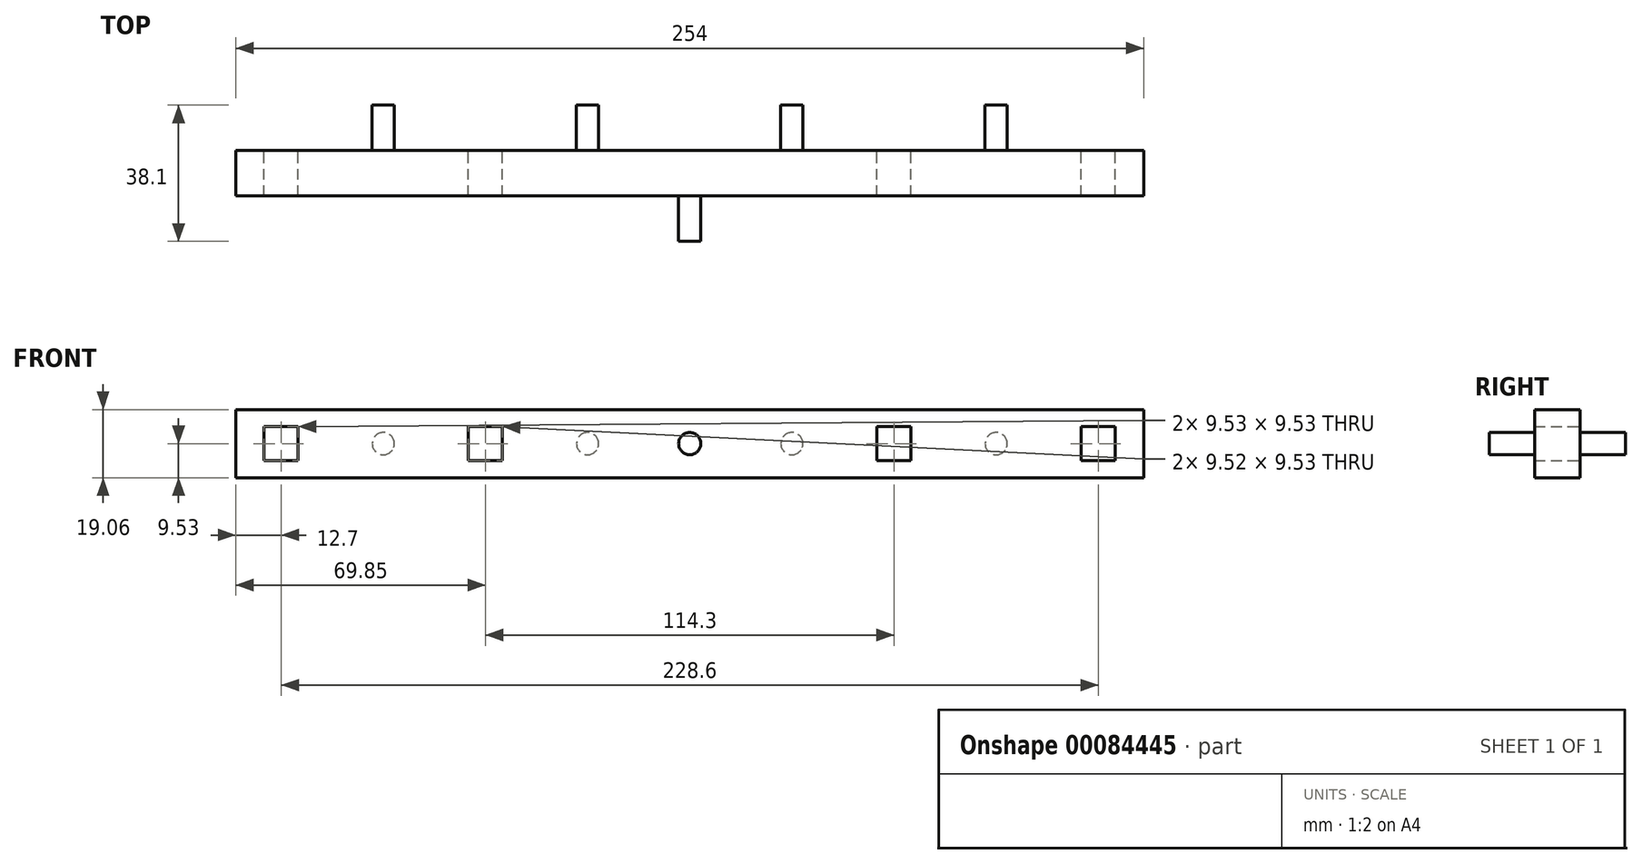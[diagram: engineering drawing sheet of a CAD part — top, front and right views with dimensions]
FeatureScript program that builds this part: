
annotation { "Feature Type Name" : "Feature", "Feature Type Description" : "" }
export const myFeature = defineFeature(function(context is Context, id is Id, definition is map)
    precondition{}
    {
        {
            var Q0;
            Q0=qCreatedBy(makeId("Front.planeOp"),FACE);
            var sketch = newSketch(context, id + "F0", { "sketchPlane" : qUnion([Q0])});
            skLineSegment(sketch, "E0.bottom", {"start": v(127, 9.53) * mm, "end": v(-127, 9.53) * mm});
            skLineSegment(sketch, "E0.top", {"start": v(127, -9.53) * mm, "end": v(-127, -9.53) * mm});
            skLineSegment(sketch, "E0.left", {"start": v(127, 9.53) * mm, "end": v(127, -9.53) * mm});
            skLineSegment(sketch, "E0.right", {"start": v(-127, 9.53) * mm, "end": v(-127, -9.53) * mm});
            skPoint(sketch, "E0.middle", {"position": v(0, 0) * mm});
            skSolve(sketch);
        }
        {
            var Q0;
            Q0 = qSketchRegion(id + "F0", true);
            extrude(context, id + "F1", {"entities" : qUnion([Q0]), "depth" : 12.7 * mm});
        }
        {
            var Q0;
            Q0=makeQuery(id+"F1.opExtrude","CAP_FACE",FACE,{"disambiguationData":[OSD([sQuery(id+"F0.wireOp",EDGE,"E0.bottom"),sQuery(id+"F0.wireOp",EDGE,"E0.top"),sQuery(id+"F0.wireOp",EDGE,"E0.left"),sQuery(id+"F0.wireOp",EDGE,"E0.right")])],"isStart":false});
            var sketch = newSketch(context, id + "F2", { "sketchPlane" : qUnion([Q0])});
            skCircle(sketch, "E1", {"center": v(0, 0) * mm, "radius": 3.11 * mm});
            skSolve(sketch);
        }
        {
            var Q0;
            Q0=makeQuery(id+"F2.imprint","IMPRINT",FACE,{"disambiguationData":[TD([[makeQuery(id+"F2.imprint","IMPRINT",EDGE,{"derivedFrom":sQuery(id+"F2.wireOp",EDGE,"E1")}),1.0]])]});
            extrude(context, id + "F3", {"entities" : qUnion([Q0]), "operationType" : NewBodyOperationType.ADD, "depth" : 12.7 * mm});
        }
        {
            var Q0;
            Q0=makeQuery(id+"F1.opExtrude","CAP_FACE",FACE,{"disambiguationData":[OSD([sQuery(id+"F0.wireOp",EDGE,"E0.bottom"),sQuery(id+"F0.wireOp",EDGE,"E0.top"),sQuery(id+"F0.wireOp",EDGE,"E0.left"),sQuery(id+"F0.wireOp",EDGE,"E0.right")])],"isStart":true});
            var sketch = newSketch(context, id + "F4", { "sketchPlane" : qUnion([Q0])});
            skPoint(sketch, "E2.middle", {"position": v(0, 0) * mm});
            skLineSegment(sketch, "E3.bottom", {"start": v(61.91, -4.76) * mm, "end": v(52.39, -4.76) * mm});
            skLineSegment(sketch, "E3.top", {"start": v(61.91, 4.76) * mm, "end": v(52.39, 4.76) * mm});
            skLineSegment(sketch, "E3.left", {"start": v(61.91, -4.76) * mm, "end": v(61.91, 4.76) * mm});
            skLineSegment(sketch, "E3.right", {"start": v(52.39, -4.76) * mm, "end": v(52.39, 4.76) * mm});
            skPoint(sketch, "E3.middle", {"position": v(57.15, 0) * mm});
            skLineSegment(sketch, "E4.bottom", {"start": v(-52.39, -4.76) * mm, "end": v(-61.91, -4.76) * mm});
            skLineSegment(sketch, "E4.top", {"start": v(-52.39, 4.76) * mm, "end": v(-61.91, 4.76) * mm});
            skLineSegment(sketch, "E4.left", {"start": v(-52.39, -4.76) * mm, "end": v(-52.39, 4.76) * mm});
            skLineSegment(sketch, "E4.right", {"start": v(-61.91, -4.76) * mm, "end": v(-61.91, 4.76) * mm});
            skPoint(sketch, "E4.middle", {"position": v(-57.15, 0) * mm});
            skLineSegment(sketch, "E5.bottom", {"start": v(-109.54, -4.76) * mm, "end": v(-119.06, -4.76) * mm});
            skLineSegment(sketch, "E5.top", {"start": v(-109.54, 4.76) * mm, "end": v(-119.06, 4.76) * mm});
            skLineSegment(sketch, "E5.left", {"start": v(-109.54, -4.76) * mm, "end": v(-109.54, 4.76) * mm});
            skLineSegment(sketch, "E5.right", {"start": v(-119.06, -4.76) * mm, "end": v(-119.06, 4.76) * mm});
            skPoint(sketch, "E5.middle", {"position": v(-114.3, 0) * mm});
            skCircle(sketch, "E6", {"center": v(-28.58, 0) * mm, "radius": 3.11 * mm});
            skCircle(sketch, "E7", {"center": v(28.58, 0) * mm, "radius": 3.11 * mm});
            skCircle(sketch, "E8", {"center": v(85.73, 0) * mm, "radius": 3.11 * mm});
            skCircle(sketch, "E9", {"center": v(-85.73, 0) * mm, "radius": 3.11 * mm});
            skLineSegment(sketch, "E10.bottom", {"start": v(109.54, 4.76) * mm, "end": v(119.06, 4.76) * mm});
            skLineSegment(sketch, "E10.top", {"start": v(109.54, -4.76) * mm, "end": v(119.06, -4.76) * mm});
            skLineSegment(sketch, "E10.left", {"start": v(109.54, 4.76) * mm, "end": v(109.54, -4.76) * mm});
            skLineSegment(sketch, "E10.right", {"start": v(119.06, 4.76) * mm, "end": v(119.06, -4.76) * mm});
            skPoint(sketch, "E10.middle", {"position": v(114.3, 0) * mm});
            skSolve(sketch);
        }
        {
            var Q0;
            Q0=makeQuery(id+"F4.imprint","IMPRINT",FACE,{"disambiguationData":[TD([[makeQuery(id+"F4.imprint","IMPRINT",EDGE,{"derivedFrom":sQuery(id+"F4.wireOp",EDGE,"E5.bottom")}),-1.0]])]});
            var Q1;
            Q1=makeQuery(id+"F4.imprint","IMPRINT",FACE,{"disambiguationData":[TD([[makeQuery(id+"F4.imprint","IMPRINT",EDGE,{"derivedFrom":sQuery(id+"F4.wireOp",EDGE,"E9")}),1.0]])]});
            var Q2;
            Q2=makeQuery(id+"F4.imprint","IMPRINT",FACE,{"disambiguationData":[TD([[makeQuery(id+"F4.imprint","IMPRINT",EDGE,{"derivedFrom":sQuery(id+"F4.wireOp",EDGE,"E4.bottom")}),-1.0]])]});
            var Q3;
            Q3=makeQuery(id+"F4.imprint","IMPRINT",FACE,{"disambiguationData":[TD([[makeQuery(id+"F4.imprint","IMPRINT",EDGE,{"derivedFrom":sQuery(id+"F4.wireOp",EDGE,"E6")}),1.0]])]});
            var Q4;
            Q4=makeQuery(id+"F4.imprint","IMPRINT",FACE,{"disambiguationData":[TD([[makeQuery(id+"F4.imprint","IMPRINT",EDGE,{"derivedFrom":sQuery(id+"F4.wireOp",EDGE,"E2.bottom")}),-1.0]])]});
            var Q5;
            Q5=makeQuery(id+"F4.imprint","IMPRINT",FACE,{"disambiguationData":[TD([[makeQuery(id+"F4.imprint","IMPRINT",EDGE,{"derivedFrom":sQuery(id+"F4.wireOp",EDGE,"E7")}),1.0]])]});
            var Q6;
            Q6=makeQuery(id+"F4.imprint","IMPRINT",FACE,{"disambiguationData":[TD([[makeQuery(id+"F4.imprint","IMPRINT",EDGE,{"derivedFrom":sQuery(id+"F4.wireOp",EDGE,"E3.bottom")}),-1.0]])]});
            var Q7;
            Q7=makeQuery(id+"F4.imprint","IMPRINT",FACE,{"disambiguationData":[TD([[makeQuery(id+"F4.imprint","IMPRINT",EDGE,{"derivedFrom":sQuery(id+"F4.wireOp",EDGE,"E8")}),1.0]])]});
            var Q8;
            Q8=makeQuery(id+"F4.imprint","IMPRINT",FACE,{"disambiguationData":[TD([[makeQuery(id+"F4.imprint","IMPRINT",EDGE,{"derivedFrom":sQuery(id+"F4.wireOp",EDGE,"E10.bottom")}),-1.0]])]});
            extrude(context, id + "F5", {"entities" : qUnion([Q0, Q1, Q2, Q3, Q4, Q5, Q6, Q7, Q8]), "operationType" : NewBodyOperationType.ADD, "depth" : 12.7 * mm});
        }
        {
            var Q0;
            Q0=makeQuery(id+"F5.opExtrude","CAP_FACE",FACE,{"disambiguationData":[OSD([sQuery(id+"F4.wireOp",EDGE,"E5.bottom"),sQuery(id+"F4.wireOp",EDGE,"E5.top"),sQuery(id+"F4.wireOp",EDGE,"E5.left"),sQuery(id+"F4.wireOp",EDGE,"E5.right")])],"isStart":false});
            var Q1;
            Q1=makeQuery(id+"F5.opExtrude","CAP_FACE",FACE,{"disambiguationData":[OSD([sQuery(id+"F4.wireOp",EDGE,"E4.bottom"),sQuery(id+"F4.wireOp",EDGE,"E4.top"),sQuery(id+"F4.wireOp",EDGE,"E4.left"),sQuery(id+"F4.wireOp",EDGE,"E4.right")])],"isStart":false});
            var Q2;
            Q2=makeQuery(id+"F5.opExtrude","CAP_FACE",FACE,{"disambiguationData":[OSD([sQuery(id+"F4.wireOp",EDGE,"E3.bottom"),sQuery(id+"F4.wireOp",EDGE,"E3.top"),sQuery(id+"F4.wireOp",EDGE,"E3.left"),sQuery(id+"F4.wireOp",EDGE,"E3.right")])],"isStart":false});
            var Q3;
            Q3=makeQuery(id+"F5.opExtrude","CAP_FACE",FACE,{"disambiguationData":[OSD([sQuery(id+"F4.wireOp",EDGE,"E10.bottom"),sQuery(id+"F4.wireOp",EDGE,"E10.top"),sQuery(id+"F4.wireOp",EDGE,"E10.left"),sQuery(id+"F4.wireOp",EDGE,"E10.right")])],"isStart":false});
            extrude(context, id + "F6", {"entities" : qUnion([Q0, Q1, Q2, Q3]), "operationType" : NewBodyOperationType.REMOVE, "oppositeDirection" : true, "depth" : 25.4 * mm});
        }
    });
